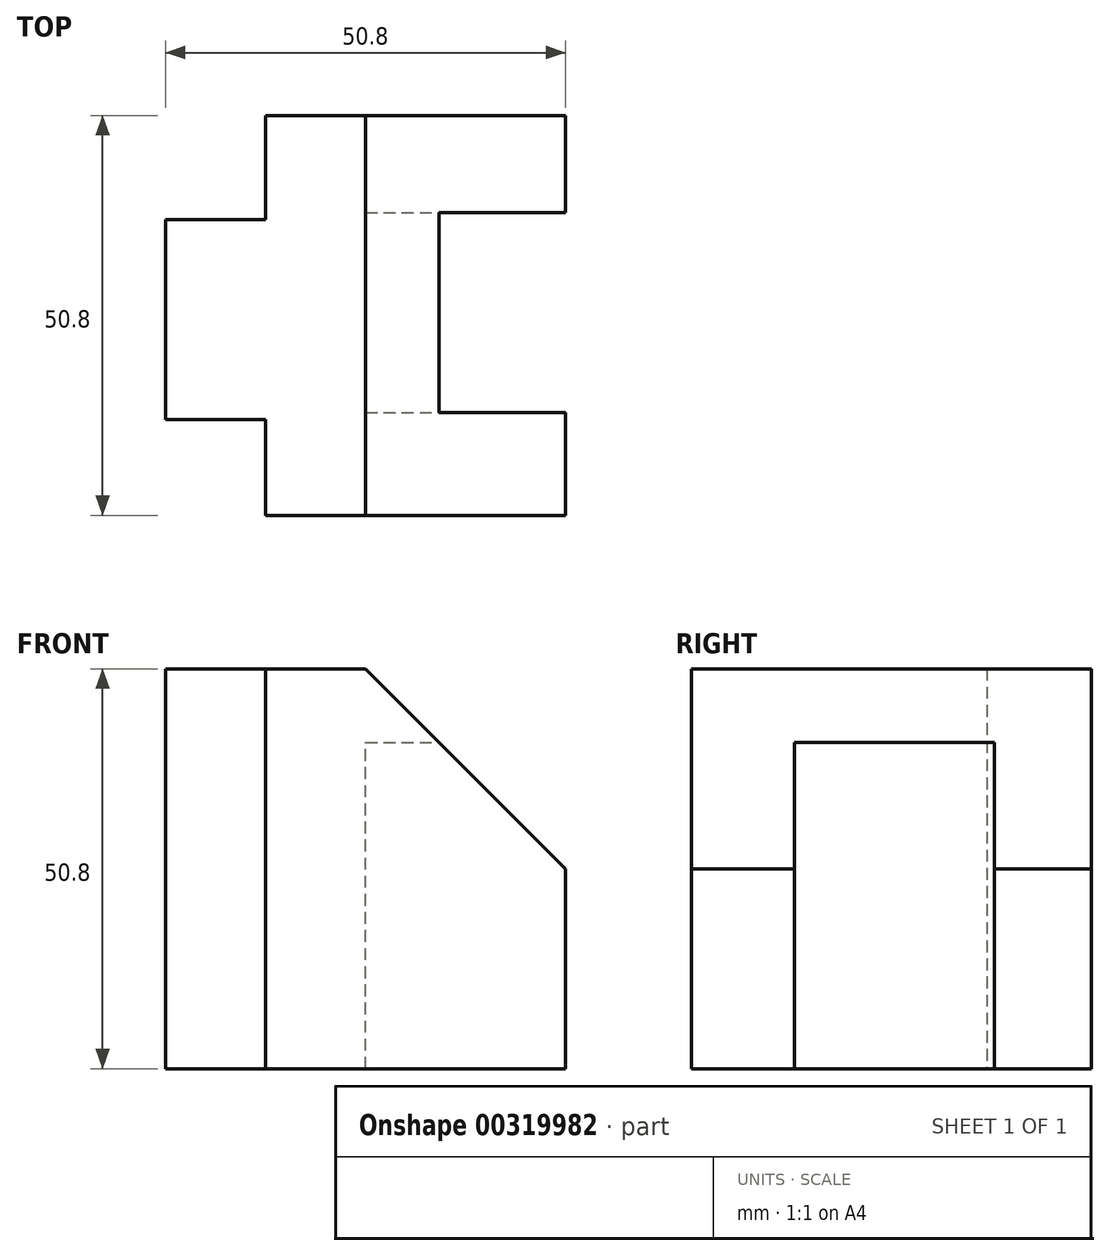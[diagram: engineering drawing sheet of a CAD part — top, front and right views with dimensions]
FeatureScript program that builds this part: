
annotation { "Feature Type Name" : "Feature", "Feature Type Description" : "" }
export const myFeature = defineFeature(function(context is Context, id is Id, definition is map)
    precondition{}
    {
        {
            var Q0;
            Q0=qCreatedBy(makeId("Top.planeOp"),FACE);
            var sketch = newSketch(context, id + "F0", { "sketchPlane" : qUnion([Q0])});
            skLineSegment(sketch, "E0", {"start": v(0, 0) * mm, "end": v(0, 50.8) * mm});
            skLineSegment(sketch, "E1", {"start": v(0, 50.8) * mm, "end": v(-12.7, 50.8) * mm});
            skLineSegment(sketch, "E2", {"start": v(-12.7, 50.8) * mm, "end": v(-12.7, 37.54) * mm});
            skLineSegment(sketch, "E3", {"start": v(-12.7, 37.54) * mm, "end": v(-25.4, 37.54) * mm});
            skLineSegment(sketch, "E4", {"start": v(-25.4, 37.54) * mm, "end": v(-25.4, 12.14) * mm});
            skLineSegment(sketch, "E5", {"start": v(-25.4, 12.14) * mm, "end": v(-12.7, 12.14) * mm});
            skLineSegment(sketch, "E6", {"start": v(-12.7, 12.14) * mm, "end": v(-12.7, 0) * mm});
            skLineSegment(sketch, "E7", {"start": v(-12.7, 0) * mm, "end": v(0, 0) * mm});
            skSolve(sketch);
        }
        {
            var Q0;
            Q0 = qSketchRegion(id + "F0", true);
            extrude(context, id + "F1", {"entities" : qUnion([Q0]), "depth" : 50.8 * mm});
        }
        {
            var Q0;
            Q0=makeQuery(id+"F1.opExtrude","SWEPT_FACE",FACE,{"disambiguationData":[OSD([sQuery(id+"F0.wireOp",EDGE,"E7")])]});
            var sketch = newSketch(context, id + "F2", { "sketchPlane" : qUnion([Q0])});
            skLineSegment(sketch, "E8", {"start": v(0, 0) * mm, "end": v(25.4, 0) * mm});
            skLineSegment(sketch, "E9", {"start": v(25.4, 0) * mm, "end": v(25.4, 25.4) * mm});
            skLineSegment(sketch, "E10", {"start": v(25.4, 25.4) * mm, "end": v(0, 50.8) * mm});
            skLineSegment(sketch, "E11", {"start": v(0, 50.8) * mm, "end": v(0, 0) * mm});
            skSolve(sketch);
        }
        {
            var Q0;
            Q0 = qSketchRegion(id + "F2", true);
            extrude(context, id + "F3", {"entities" : qUnion([Q0]), "operationType" : NewBodyOperationType.ADD, "oppositeDirection" : true, "depth" : 50.8 * mm});
        }
        {
            var Q0;
            Q0=makeQuery(id+"F3.opExtrude","SWEPT_FACE",FACE,{"disambiguationData":[OSD([sQuery(id+"F2.wireOp",EDGE,"E9")])]});
            var sketch = newSketch(context, id + "F4", { "sketchPlane" : qUnion([Q0])});
            skLineSegment(sketch, "E12.bottom", {"start": v(13.08, 0) * mm, "end": v(38.48, 0) * mm});
            skLineSegment(sketch, "E12.top", {"start": v(13.08, 41.45) * mm, "end": v(38.48, 41.45) * mm});
            skLineSegment(sketch, "E12.left", {"start": v(13.08, 0) * mm, "end": v(13.08, 41.45) * mm});
            skLineSegment(sketch, "E12.right", {"start": v(38.48, 0) * mm, "end": v(38.48, 41.45) * mm});
            skSolve(sketch);
        }
        {
            var Q0;
            Q0 = qSketchRegion(id + "F4", true);
            extrude(context, id + "F5", {"entities" : qUnion([Q0]), "operationType" : NewBodyOperationType.REMOVE, "oppositeDirection" : true, "depth" : 25.4 * mm});
        }
    });
